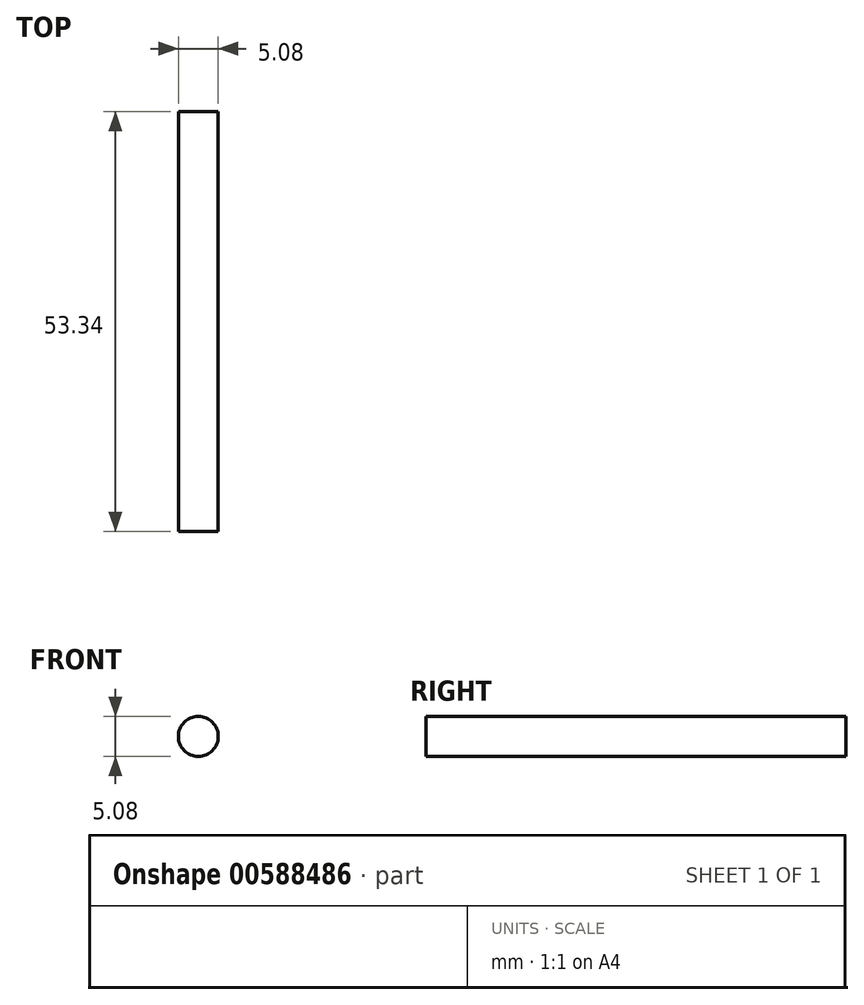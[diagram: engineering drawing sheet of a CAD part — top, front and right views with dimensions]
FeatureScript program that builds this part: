
annotation { "Feature Type Name" : "Feature", "Feature Type Description" : "" }
export const myFeature = defineFeature(function(context is Context, id is Id, definition is map)
    precondition{}
    {
        {
            var Q0;
            Q0=qCreatedBy(makeId("Front.planeOp"),FACE);
            var sketch = newSketch(context, id + "F0", { "sketchPlane" : qUnion([Q0])});
            skCircle(sketch, "E0", {"center": v(0, 0) * mm, "radius": 2.54 * mm});
            skSolve(sketch);
        }
        {
            var Q0;
            Q0 = qSketchRegion(id + "F0", true);
            extrude(context, id + "F1", {"entities" : qUnion([Q0]), "endBound" : BoundingType.SYMMETRIC, "depth" : 53.34 * mm, "offsetDistance" : 25.4 * mm});
        }
    });
